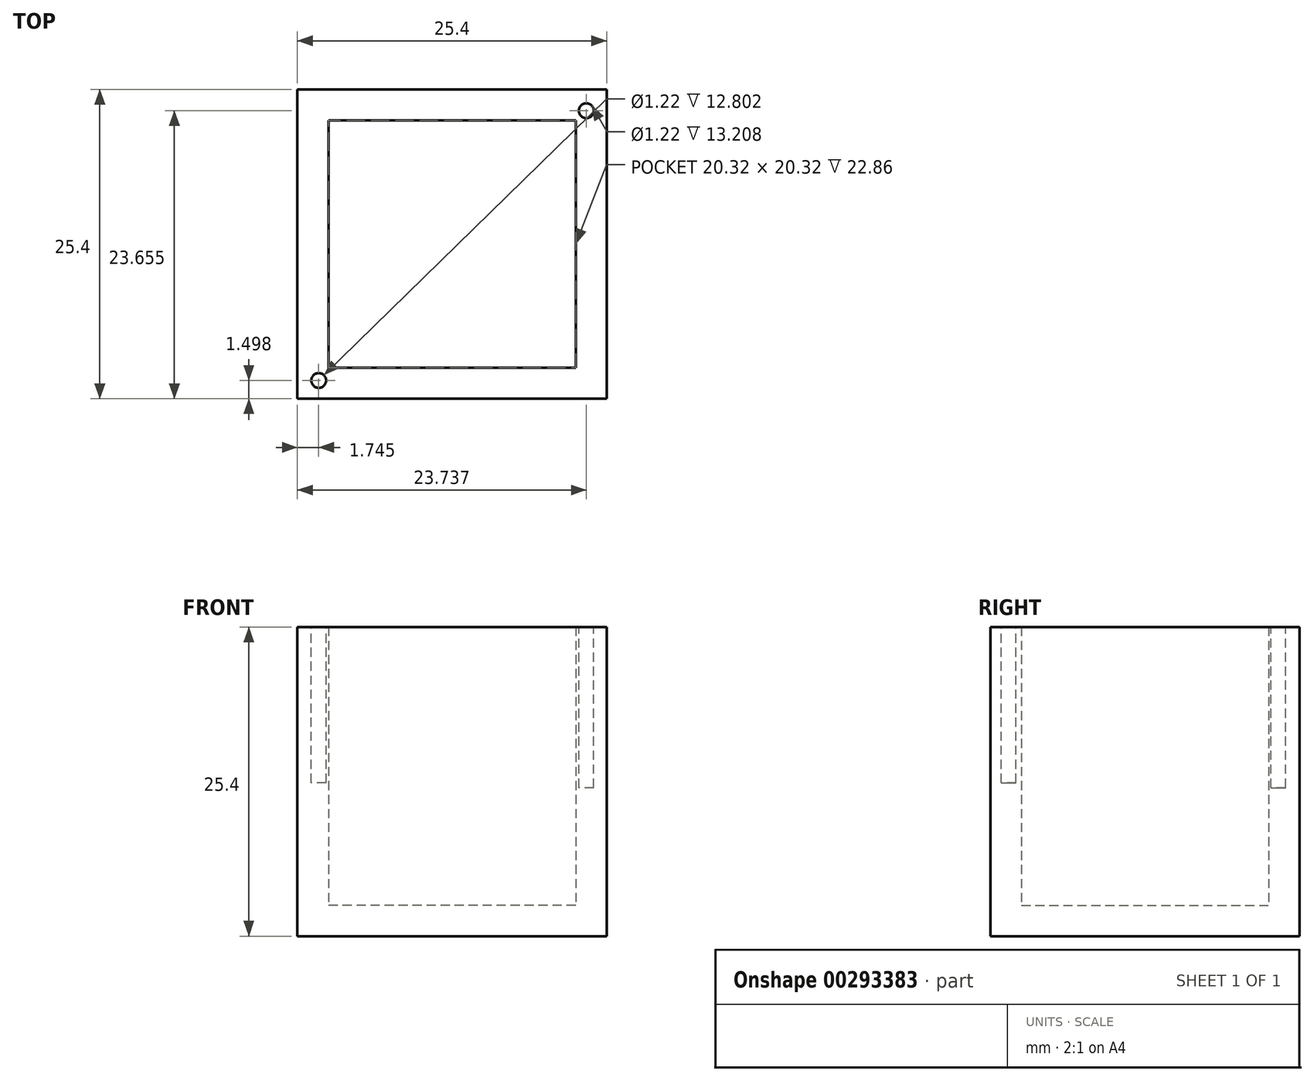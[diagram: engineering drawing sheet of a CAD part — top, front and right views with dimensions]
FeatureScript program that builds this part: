
annotation { "Feature Type Name" : "Feature", "Feature Type Description" : "" }
export const myFeature = defineFeature(function(context is Context, id is Id, definition is map)
    precondition{}
    {
        {
            var Q0;
            Q0=qCreatedBy(makeId("Front.planeOp"),FACE);
            var sketch = newSketch(context, id + "F0", { "sketchPlane" : qUnion([Q0])});
            skLineSegment(sketch, "E0.bottom", {"start": v(12.7, 12.7) * mm, "end": v(-12.7, 12.7) * mm});
            skLineSegment(sketch, "E0.top", {"start": v(12.7, -12.7) * mm, "end": v(-12.7, -12.7) * mm});
            skLineSegment(sketch, "E0.left", {"start": v(12.7, 12.7) * mm, "end": v(12.7, -12.7) * mm});
            skLineSegment(sketch, "E0.right", {"start": v(-12.7, 12.7) * mm, "end": v(-12.7, -12.7) * mm});
            skPoint(sketch, "E0.middle", {"position": v(0, 0) * mm});
            skSolve(sketch);
        }
        {
            var Q0;
            Q0=makeQuery(id+"F0.imprint","IMPRINT",FACE,{"disambiguationData":[TD([[makeQuery(id+"F0.imprint","IMPRINT",EDGE,{"derivedFrom":sQuery(id+"F0.wireOp",EDGE,"E0.bottom")}),1.0]])]});
            extrude(context, id + "F1", {"entities" : qUnion([Q0]), "depth" : 25.4 * mm});
        }
        {
            var Q0;
            Q0=makeQuery(id+"F1.opExtrude","SWEPT_FACE",FACE,{"disambiguationData":[OSD([sQuery(id+"F0.wireOp",EDGE,"E0.bottom")])]});
            shell(context, id + "F2", {"entities" : qUnion([Q0]), "thickness" : 2.54 * mm});
        }
        {
            var Q0;
            Q0=makeQuery(id+"F1.opExtrude","SWEPT_FACE",FACE,{"disambiguationData":[OSD([sQuery(id+"F0.wireOp",EDGE,"E0.bottom")])]});
            var sketch = newSketch(context, id + "F3", { "sketchPlane" : qUnion([Q0])});
            skCircle(sketch, "E1", {"center": v(-10.96, -23.9) * mm, "radius": 0.6 * mm});
            skSolve(sketch);
        }
        {
            var Q0;
            Q0 = qSketchRegion(id + "F3", true);
            extrude(context, id + "F4", {"entities" : qUnion([Q0]), "operationType" : NewBodyOperationType.REMOVE, "oppositeDirection" : true, "depth" : 12.8 * mm});
        }
        {
            var Q0;
            Q0=makeQuery(id+"F1.opExtrude","SWEPT_FACE",FACE,{"disambiguationData":[OSD([sQuery(id+"F0.wireOp",EDGE,"E0.bottom")])]});
            var sketch = newSketch(context, id + "F5", { "sketchPlane" : qUnion([Q0])});
            skCircle(sketch, "E2", {"center": v(11.04, -1.75) * mm, "radius": 0.6 * mm});
            skSolve(sketch);
        }
        {
            var Q0;
            Q0=makeQuery(id+"F5.imprint","IMPRINT",FACE,{"disambiguationData":[TD([[makeQuery(id+"F5.imprint","IMPRINT",EDGE,{"derivedFrom":sQuery(id+"F5.wireOp",EDGE,"E2")}),1.0]])]});
            extrude(context, id + "F6", {"entities" : qUnion([Q0]), "operationType" : NewBodyOperationType.REMOVE, "oppositeDirection" : true, "depth" : 13.2 * mm});
        }
    });
